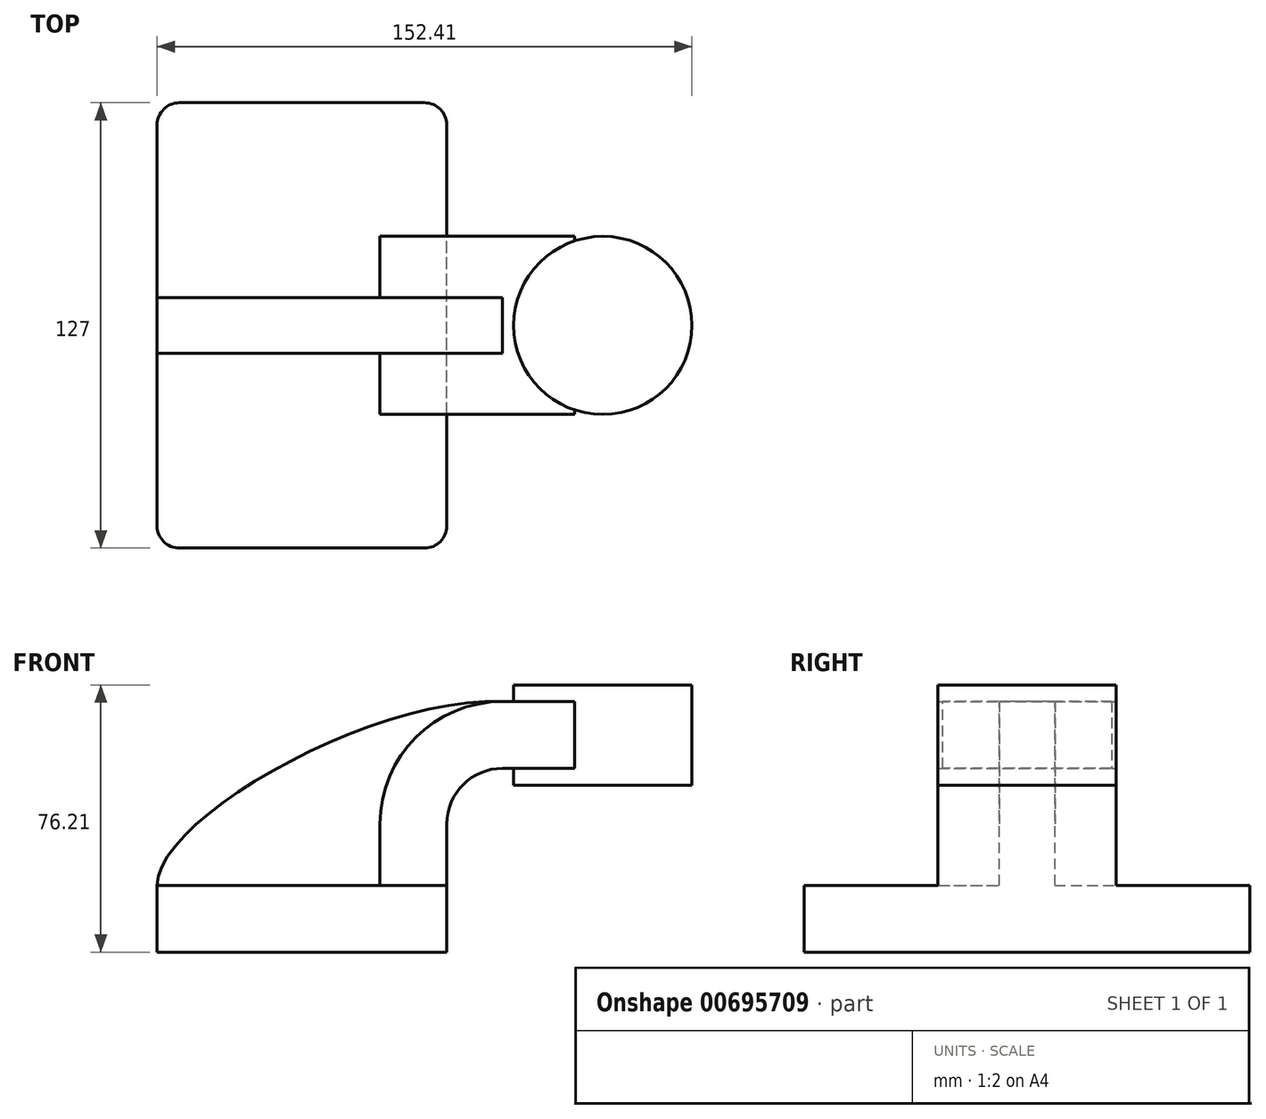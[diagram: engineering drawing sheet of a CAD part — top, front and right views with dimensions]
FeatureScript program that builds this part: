
annotation { "Feature Type Name" : "Feature", "Feature Type Description" : "" }
export const myFeature = defineFeature(function(context is Context, id is Id, definition is map)
    precondition{}
    {
        {
            var Q0;
            Q0=qCreatedBy(makeId("Front.planeOp"),FACE);
            var sketch = newSketch(context, id + "F0", { "sketchPlane" : qUnion([Q0])});
            skLineSegment(sketch, "E0.bottom", {"start": v(-41.28, 9.52) * mm, "end": v(41.28, 9.52) * mm});
            skLineSegment(sketch, "E0.top", {"start": v(-41.28, -9.52) * mm, "end": v(41.27, -9.52) * mm});
            skLineSegment(sketch, "E0.left", {"start": v(-41.28, 9.52) * mm, "end": v(-41.28, -9.52) * mm});
            skLineSegment(sketch, "E0.right", {"start": v(41.28, 9.52) * mm, "end": v(41.27, -9.52) * mm});
            skPoint(sketch, "E0.middle", {"position": v(0, 0) * mm});
            skLineSegment(sketch, "E1.bottom", {"start": v(60.33, 38.1) * mm, "end": v(111.12, 38.1) * mm});
            skLineSegment(sketch, "E1.top", {"start": v(60.32, 66.68) * mm, "end": v(111.12, 66.68) * mm});
            skLineSegment(sketch, "E1.left", {"start": v(60.33, 38.1) * mm, "end": v(60.32, 66.68) * mm});
            skLineSegment(sketch, "E1.right", {"start": v(111.12, 38.1) * mm, "end": v(111.12, 66.68) * mm});
            skPoint(sketch, "E1.middle", {"position": v(85.72, 52.39) * mm});
            skLineSegment(sketch, "E2", {"start": v(41.28, 9.52) * mm, "end": v(41.28, 27) * mm});
            skArc(sketch, "E3", {"start": v(41.27, 27) * mm, "mid": v(45.92, 38.23) * mm, "end": v(57.15, 42.88) * mm});
            skLineSegment(sketch, "E4", {"start": v(57.15, 42.88) * mm, "end": v(77.67, 42.88) * mm});
            skLineSegment(sketch, "E5.0", {"start": v(57.15, 61.93) * mm, "end": v(77.67, 61.93) * mm});
            skArc(sketch, "E5.1", {"start": v(22.22, 27) * mm, "mid": v(32.45, 51.7) * mm, "end": v(57.15, 61.93) * mm});
            skLineSegment(sketch, "E5.2", {"start": v(22.22, 9.52) * mm, "end": v(22.22, 27) * mm});
            skLineSegment(sketch, "E6", {"start": v(77.67, 61.93) * mm, "end": v(77.67, 42.88) * mm});
            skLineSegment(sketch, "E7", {"start": v(22.22, 9.52) * mm, "end": v(41.28, 9.52) * mm});
            skFitSpline(sketch, "E8", {"points": [v(-41.28, 9.52) * mm, v(57.15, 61.93) * mm], "startDerivative": vector(-0.22, 57.78) * mm, "endDerivative": vector(110.21, -4.84) * mm});
            skLineSegment(sketch, "E9", {"start": v(85.72, 66.68) * mm, "end": v(85.72, 38.1) * mm});
            skSolve(sketch);
        }
        {
            var Q0;
            Q0=makeQuery(id+"F0.imprint","IMPRINT",FACE,{"disambiguationData":[TD([[makeQuery(id+"F0.imprint","IMPRINT",EDGE,{"derivedFrom":sQuery(id+"F0.wireOp",EDGE,"E0.bottom")}),-1.0]])]});
            extrude(context, id + "F1", {"entities" : qUnion([Q0]), "endBound" : BoundingType.SYMMETRIC, "depth" : 127 * mm, "offsetDistance" : 25.4 * mm});
        }
        {
            var Q0;
            Q0=makeQuery(id+"F0.imprint","IMPRINT",FACE,{"disambiguationData":[TD([[makeQuery(id+"F0.imprint","IMPRINT",EDGE,{"derivedFrom":sQuery(id+"F0.wireOp",EDGE,"E2")}),1.0]])]});
            var Q1;
            {var subQ5=sQuery(id+"F0.wireOp",EDGE,"E6");Q1=makeQuery(id+"F0.imprint","IMPRINT",FACE,{"disambiguationData":[TD([[makeQuery(id+"F0.imprint","IMPRINT",EDGE,{"derivedFrom":subQ5}),-1.0]])]});}
            extrude(context, id + "F2", {"entities" : qUnion([Q0, Q1]), "operationType" : NewBodyOperationType.ADD, "endBound" : BoundingType.SYMMETRIC, "depth" : 50.8 * mm, "offsetDistance" : 25.4 * mm});
        }
        {
            var Q0;
            Q0=makeQuery(id+"F0.imprint","IMPRINT",FACE,{"disambiguationData":[TD([[makeQuery(id+"F0.imprint","IMPRINT",EDGE,{"derivedFrom":sQuery(id+"F0.wireOp",EDGE,"E0.bottom")}),1.0]])]});
            extrude(context, id + "F3", {"entities" : qUnion([Q0]), "operationType" : NewBodyOperationType.ADD, "endBound" : BoundingType.SYMMETRIC, "depth" : 15.88 * mm, "offsetDistance" : 25.4 * mm});
        }
        {
            var Q0;
            {var subQ0=sQuery(id+"F0.wireOp",EDGE,"E1.right");Q0=makeQuery(id+"F0.imprint","IMPRINT",FACE,{"disambiguationData":[TD([[makeQuery(id+"F0.imprint","IMPRINT",EDGE,{"derivedFrom":subQ0}),1.0]])]});}
            var Q1;
            Q1=sQuery(id+"F0.wireOp",EDGE,"E9");
            revolve(context, id + "F4", {"operationType" : NewBodyOperationType.ADD, "entities" : qUnion([Q0]), "axis" : qUnion([Q1]), "revolveType" : RevolveType.FULL});
        }
        {
            var Q0;
            Q0=makeQuery(id+"F1.opExtrude","CAP_EDGE",EDGE,{"disambiguationData":[OSD([sQuery(id+"F0.wireOp",EDGE,"E0.right")])],"isStart":false});
            var Q1;
            Q1=makeQuery(id+"F1.opExtrude","CAP_EDGE",EDGE,{"disambiguationData":[OSD([sQuery(id+"F0.wireOp",EDGE,"E0.left")])],"isStart":false});
            var Q2;
            Q2=makeQuery(id+"F1.opExtrude","CAP_EDGE",EDGE,{"disambiguationData":[OSD([sQuery(id+"F0.wireOp",EDGE,"E0.right")])],"isStart":true});
            var Q3;
            Q3=makeQuery(id+"F1.opExtrude","CAP_EDGE",EDGE,{"disambiguationData":[OSD([sQuery(id+"F0.wireOp",EDGE,"E0.left")])],"isStart":true});
            fillet(context, id + "F5", {"entities" : qUnion([Q0, Q1, Q2, Q3]), "radius" : 6.35 * mm, "tangentPropagation" : true, "allowEdgeOverflow" : false});
        }
    });
